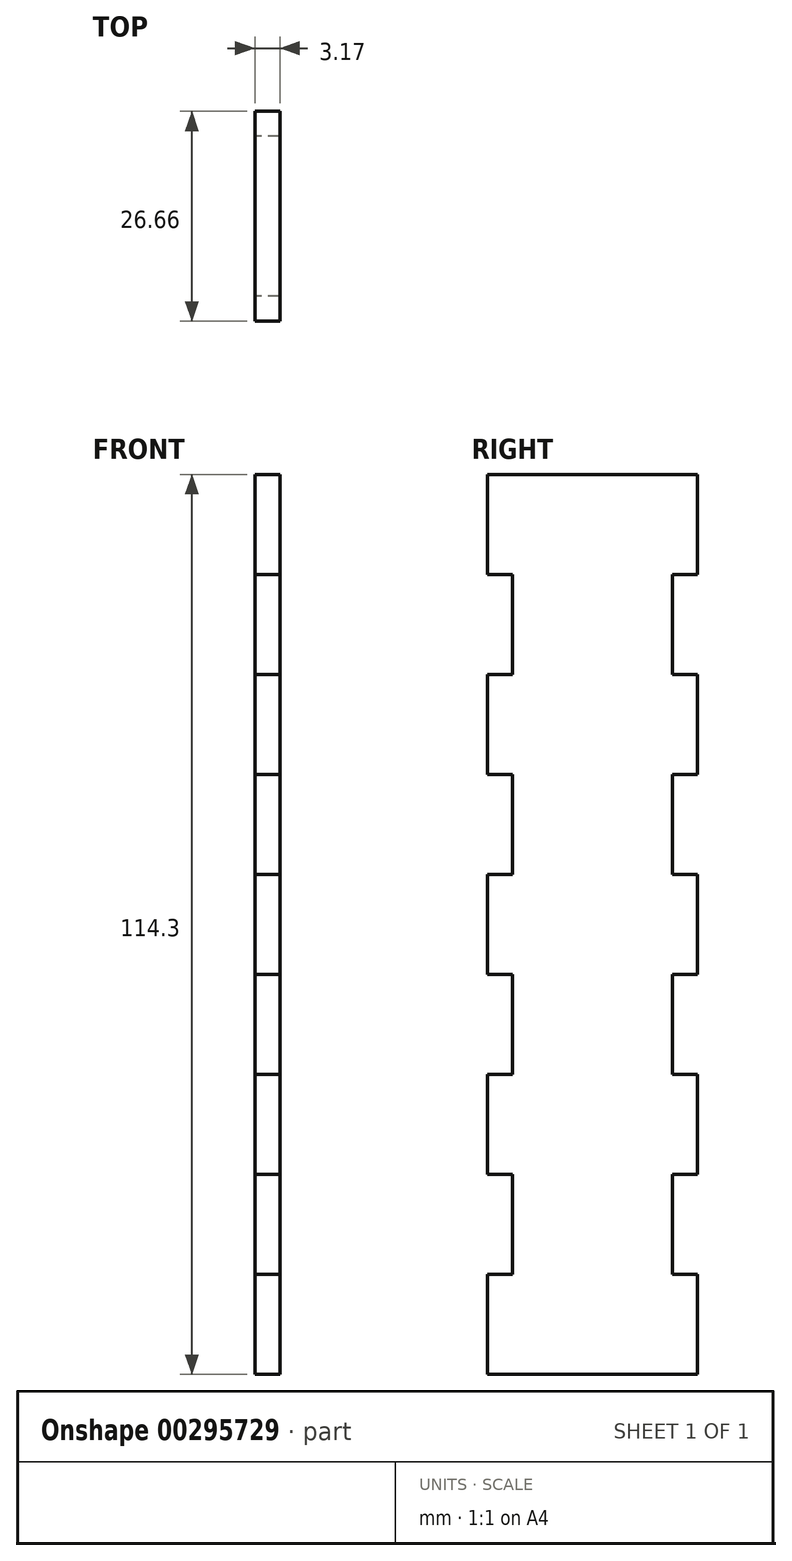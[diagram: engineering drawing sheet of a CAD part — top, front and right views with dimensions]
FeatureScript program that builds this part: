
annotation { "Feature Type Name" : "Feature", "Feature Type Description" : "" }
export const myFeature = defineFeature(function(context is Context, id is Id, definition is map)
    precondition{}
    {
        {
            var Q0;
            Q0=qCreatedBy(makeId("Right.planeOp"),FACE);
            var sketch = newSketch(context, id + "F0", { "sketchPlane" : qUnion([Q0])});
            skLineSegment(sketch, "E0.top", {"start": v(13.34, 57.15) * mm, "end": v(-13.33, 57.15) * mm, "construction": true});
            skLineSegment(sketch, "E0.left", {"start": v(13.33, -57.15) * mm, "end": v(13.34, 57.15) * mm, "construction": true});
            skPoint(sketch, "E0.middle", {"position": v(0, 0) * mm});
            skLineSegment(sketch, "E1", {"start": v(-13.33, 57.15) * mm, "end": v(-13.33, 44.45) * mm});
            skLineSegment(sketch, "E2", {"start": v(-13.33, 44.45) * mm, "end": v(-10.16, 44.45) * mm});
            skLineSegment(sketch, "E3", {"start": v(-10.16, 44.45) * mm, "end": v(-10.16, 31.75) * mm});
            skLineSegment(sketch, "E4", {"start": v(-10.16, 31.75) * mm, "end": v(-13.33, 31.75) * mm});
            skLineSegment(sketch, "E5", {"start": v(-13.33, 31.75) * mm, "end": v(-13.34, 19.05) * mm});
            skLineSegment(sketch, "E6", {"start": v(-13.33, 19.05) * mm, "end": v(-10.16, 19.05) * mm});
            skLineSegment(sketch, "E7", {"start": v(-10.16, 19.05) * mm, "end": v(-10.16, 6.35) * mm});
            skLineSegment(sketch, "E8", {"start": v(-10.16, 6.35) * mm, "end": v(-13.33, 6.35) * mm});
            skLineSegment(sketch, "E9", {"start": v(-13.34, 6.35) * mm, "end": v(-13.34, -6.35) * mm});
            skLineSegment(sketch, "E10.MirrorCS", {"start": v(-13.34, -6.35) * mm, "end": v(-13.34, 6.35) * mm});
            skLineSegment(sketch, "E11.MirrorCS", {"start": v(13.34, -57.15) * mm, "end": v(-13.33, -57.15) * mm, "construction": true});
            skLineSegment(sketch, "E12.MirrorCS", {"start": v(-13.34, 57.15) * mm, "end": v(-13.33, -57.15) * mm, "construction": true});
            skLineSegment(sketch, "E13.MirrorCS", {"start": v(-10.16, -6.35) * mm, "end": v(-13.33, -6.35) * mm});
            skLineSegment(sketch, "E14.MirrorCS", {"start": v(-13.33, -19.05) * mm, "end": v(-10.16, -19.05) * mm});
            skLineSegment(sketch, "E15.MirrorCS", {"start": v(-10.16, -19.05) * mm, "end": v(-10.16, -6.35) * mm});
            skLineSegment(sketch, "E16.MirrorCS", {"start": v(-13.33, -44.45) * mm, "end": v(-10.16, -44.45) * mm});
            skLineSegment(sketch, "E17.MirrorCS", {"start": v(-10.16, -44.45) * mm, "end": v(-10.16, -31.75) * mm});
            skLineSegment(sketch, "E18.MirrorCS", {"start": v(-10.16, -31.75) * mm, "end": v(-13.33, -31.75) * mm});
            skLineSegment(sketch, "E19.MirrorCS", {"start": v(-13.33, -57.15) * mm, "end": v(-13.33, -44.45) * mm});
            skLineSegment(sketch, "E20.MirrorCS", {"start": v(-13.33, -31.75) * mm, "end": v(-13.34, -19.05) * mm});
            skLineSegment(sketch, "E21.MirrorCS", {"start": v(10.16, -31.75) * mm, "end": v(13.33, -31.75) * mm});
            skLineSegment(sketch, "E22.MirrorCS", {"start": v(13.33, -44.45) * mm, "end": v(10.16, -44.45) * mm});
            skLineSegment(sketch, "E23.MirrorCS", {"start": v(13.33, -19.05) * mm, "end": v(10.16, -19.05) * mm});
            skLineSegment(sketch, "E24.MirrorCS", {"start": v(10.16, 31.75) * mm, "end": v(13.33, 31.75) * mm});
            skLineSegment(sketch, "E25.MirrorCS", {"start": v(10.16, -6.35) * mm, "end": v(13.33, -6.35) * mm});
            skLineSegment(sketch, "E26.MirrorCS", {"start": v(13.33, 19.05) * mm, "end": v(10.16, 19.05) * mm});
            skLineSegment(sketch, "E27.MirrorCS", {"start": v(13.33, 44.45) * mm, "end": v(10.16, 44.45) * mm});
            skLineSegment(sketch, "E28.MirrorCS", {"start": v(10.16, 6.35) * mm, "end": v(13.33, 6.35) * mm});
            skLineSegment(sketch, "E29.MirrorCS", {"start": v(13.34, 6.35) * mm, "end": v(13.34, -6.35) * mm});
            skLineSegment(sketch, "E30.MirrorCS", {"start": v(13.33, -31.75) * mm, "end": v(13.34, -19.05) * mm});
            skLineSegment(sketch, "E31.MirrorCS", {"start": v(10.16, -19.05) * mm, "end": v(10.16, -6.35) * mm});
            skLineSegment(sketch, "E32.MirrorCS", {"start": v(13.33, 57.15) * mm, "end": v(13.33, 44.45) * mm});
            skLineSegment(sketch, "E33.MirrorCS", {"start": v(13.33, 31.75) * mm, "end": v(13.34, 19.05) * mm});
            skLineSegment(sketch, "E34.MirrorCS", {"start": v(10.16, -44.45) * mm, "end": v(10.16, -31.75) * mm});
            skLineSegment(sketch, "E35.MirrorCS", {"start": v(10.16, 44.45) * mm, "end": v(10.16, 31.75) * mm});
            skLineSegment(sketch, "E36.MirrorCS", {"start": v(13.34, -6.35) * mm, "end": v(13.34, 6.35) * mm});
            skLineSegment(sketch, "E37.MirrorCS", {"start": v(10.16, 19.05) * mm, "end": v(10.16, 6.35) * mm});
            skLineSegment(sketch, "E38.MirrorCS", {"start": v(13.33, -57.15) * mm, "end": v(13.33, -44.45) * mm});
            skLineSegment(sketch, "E39", {"start": v(-13.33, 57.15) * mm, "end": v(13.34, 57.15) * mm});
            skLineSegment(sketch, "E40", {"start": v(-13.33, -57.15) * mm, "end": v(13.33, -57.15) * mm});
            skSolve(sketch);
        }
        {
            var Q0;
            Q0 = qSketchRegion(id + "F0", true);
            extrude(context, id + "F1", {"entities" : qUnion([Q0]), "depth" : 3.17 * mm});
        }
    });
